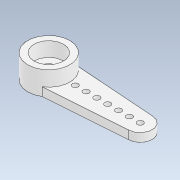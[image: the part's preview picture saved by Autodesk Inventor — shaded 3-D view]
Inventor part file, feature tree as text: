
AUTODESK INVENTOR PART (.ipt)
format: ipt  version: 2020.2 (Build 242310000, 310)  size: 139,776 bytes
history: native  units: in
note: dims shown in document units (in); Inventor stores cm internally (conversion verified against a paired STEP export)
features: projected_geometry x2, extrude x1, sketch x1, other x1
ambient origin geometry x8: Origin, YZ Plane, XZ Plane, XY Plane, X Axis, Y Axis, Z Axis, Center Point
bodies: Solid1 (feature_tree)
feature tree (5):
  extrude  "Extrusion1"  [1 undecoded]
  sketch  "Sketch1"  dims[d0=0.0in d1=0.0in]
  projected_geometry  "Projected Loop1"
  projected_geometry  "Projected Loop2"
  other  "Cut-Extrude4"
note: 1 required parameter value undecoded (feature->parameter linkage not recoverable at this tier; creation-order binding heuristic only, values carry confidence <= 0.55)
